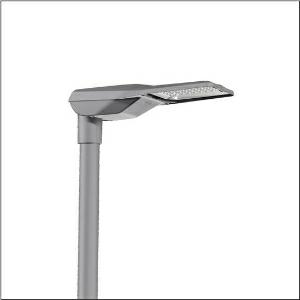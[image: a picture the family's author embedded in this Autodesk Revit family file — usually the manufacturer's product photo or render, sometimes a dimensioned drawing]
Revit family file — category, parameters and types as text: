
# Revit family: streetlight_sl_21_iq_mini___st0_8a_5xe2c61g08hb_b958
name_source: partatom
category: Lighting Fixtures
units: mm (PartAtom-declared; Revit-internal decimal feet)

## family parameters
Cut with Voids When Loaded = No
Host = Face
Light Source = No
Part Type = Normal
Room Calculation Point = No
Round Connector Dimension = Use Diameter
Shared = No

## types (1)
- --- (1 x LED, 8480 lm, 70.9 W, 2700K)
    Apparent Load = 71 VA
    CIE Flux Codes = 38 75 97 100 100
    Color Rendering = 70
    Color Temperature = 2700K
    Default Elevation = 1800 mm
    Description = Streetlight SL 21 iQ mini, mast luminaire, primary light control with lens, of PMMA, primary optical cover: cover, of toughened safety glass, transparent, light distribution: ST0.8a, light emission: direct distribution, primary light characteristic: asymmetric, installation type: post-top, side-entry, LED, High Power LED, rated luminous flux: 8.480lm, luminous efficacy: 120lm/W, light colour: 727, colour temperature: 2700K, control gear: iQ Street-Remote, control: Street-Remote, Auto-Match, Temp-Guard, Lumen-Switch, Night-Set, Smart-Wire, Light-Fading, Desk-Remote (wireless, voltage-free reading and setting of iQ features in the workshop via application-optimized NFC function/RFID function), optimised constant luminous flux control (CLO 2.0), pre-setting: linear dimming characteristic, mains connection: 220..240V, AC, 50/60Hz, start of lifetime: 71W, end of service life: 75W, reduction: 31W, luminaire housing, of diecast aluminium, powder-coated, Siteco® metallic grey (DB 702S), corrosivity category C5 mid according to DIN EN ISO 12944, please order mast flange separately, inclination adjustable: 0°, 5°, 10°, 15°, sealing non-destructively replaceable, multi-level sealing system, length: 628mm, width: 235mm, height: 110mm, mast flange for spigot size: 42mm (side-entry): 5XC10008XM4, 60/48mm (side-entry/post-top): 5XC10108XM2, 76/60mm (side-entry/post-top): 5XC10108XM1, mounting height: 4..8m, protection rating (complete): IP66, insulation class (complete): insulation class II (safety insulation), certification: CE, ENEC, ENEC+, VDE, impact resistance: IK10, permissible operating ambient temperature for outdoor applications: -40..+50°C, standard-compliant lighting for roads and squares, packaging unit: 1 piece

Light Distribution: ST0.8a
    Height = 110 mm
    Lamp = 1 x LED
    Lamp Light Flux = 8480 lm
    Lamp Power = 70.9 W
    Lamp count = 1
    Length = 625 mm
    Luminous efficacy = 120 lm/W
    Manufacturer = Siteco
    ModVariant = No
    Model = 5XE2C61G08HB
    Number of Poles = 1
    OnlyDefault = Yes
    Power Factor = 1
    Product Name = Streetlight SL 21 iQ mini | ST0.8a
    Product group = mast luminaire | pylon top
    ProductGroupID = 6100
    Protection Class = Protection class II
    Protection Degree = IP 66
    RLX_Detail_Level = 1
    RLX_Emergency_Light_Flux = 0 lm
    RLX_Emergency_Type = 0
    RLX_Emergency_Type_DB = No
    RlxData = <blob elided: 26293 chars, md5=a5401b6a>
    Socket = socket
    Standby Power = 0 W
    System Light Flux = 8480 lm
    System Power = 71 W
    Type Comments = factory setting: luminous flux: 100 % | dim-lin: 254 | 711 mA
    Type Image = l_1003519.jpg
    URL = http://relux.com
    VarID = @adj_157504
    Voltage = 0 V
    Weight = 0.00 kg
    Width = 234 mm

## geometry (parser evidence)
native form markers: Blend x4, Sweep x10
no freeform markers — native parametric forms only
